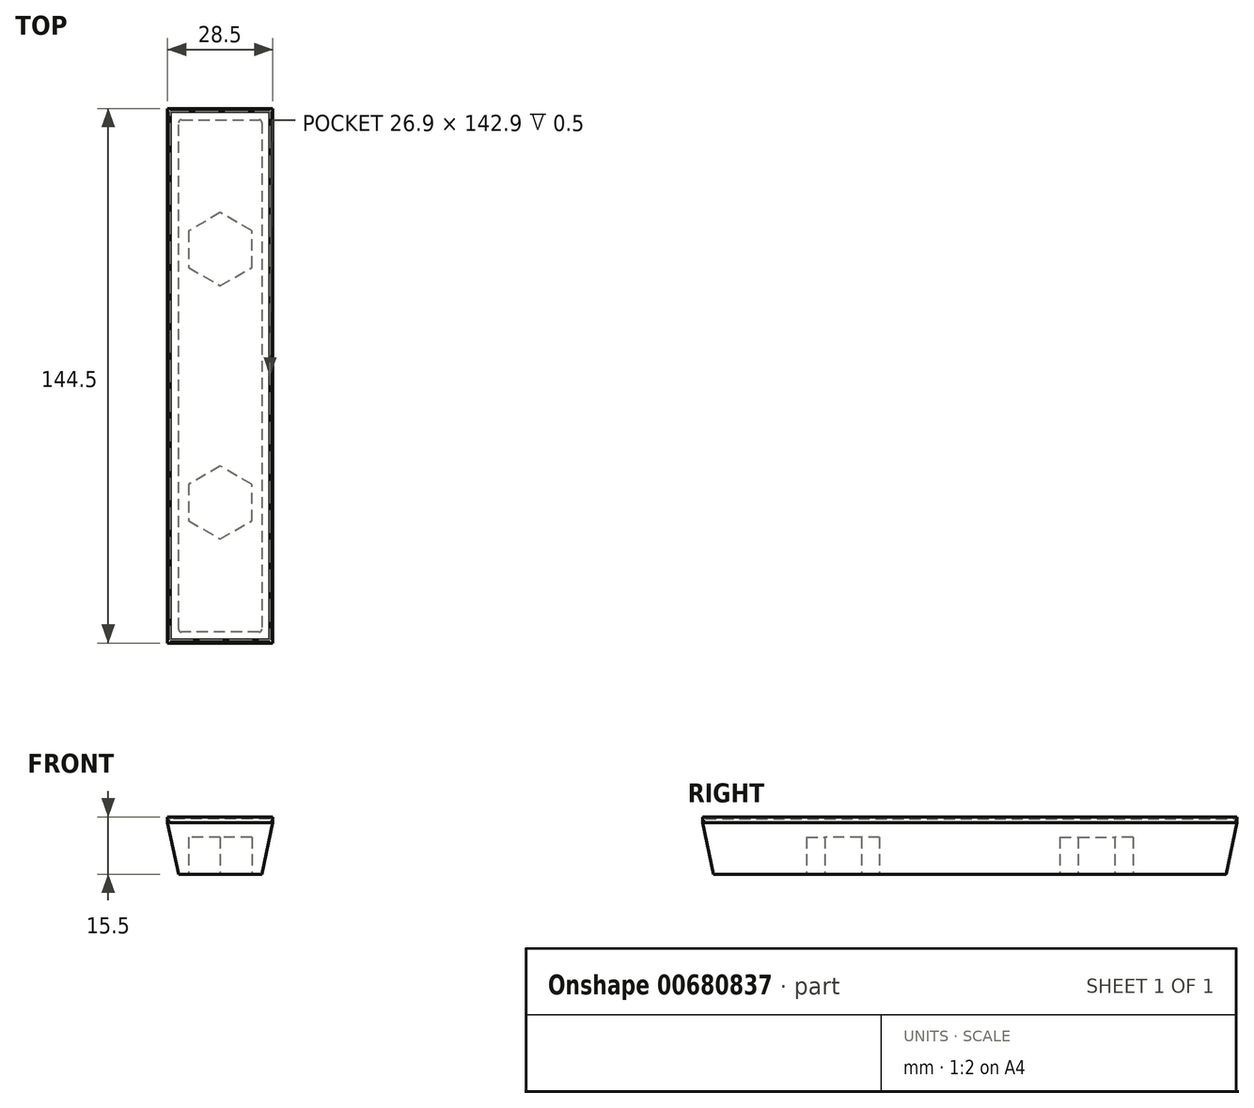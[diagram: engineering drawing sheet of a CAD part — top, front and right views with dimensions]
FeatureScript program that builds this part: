
annotation { "Feature Type Name" : "Feature", "Feature Type Description" : "" }
export const myFeature = defineFeature(function(context is Context, id is Id, definition is map)
    precondition{}
    {
        {
            assignVariable(context, id + "F0", {"name" : "h", "anyValue" : 15});
        }
        {
            var Q0;
            Q0=qCreatedBy(makeId("Top.planeOp"),FACE);
            var sketch = newSketch(context, id + "F1", { "sketchPlane" : qUnion([Q0])});
            skLineSegment(sketch, "E0.bottom", {"start": v(-14.25, -72.25) * mm, "end": v(14.25, -72.25) * mm});
            skLineSegment(sketch, "E0.top", {"start": v(-14.25, 72.25) * mm, "end": v(14.25, 72.25) * mm});
            skLineSegment(sketch, "E0.left", {"start": v(-14.25, -72.25) * mm, "end": v(-14.25, 72.25) * mm});
            skLineSegment(sketch, "E0.right", {"start": v(14.25, -72.25) * mm, "end": v(14.25, 72.25) * mm});
            skPoint(sketch, "E0.middle", {"position": v(0, 0) * mm});
            skLineSegment(sketch, "E1.bottom", {"start": v(13.45, -71.45) * mm, "end": v(-13.45, -71.45) * mm});
            skLineSegment(sketch, "E1.top", {"start": v(13.45, 71.45) * mm, "end": v(-13.45, 71.45) * mm});
            skLineSegment(sketch, "E1.left", {"start": v(13.45, -71.45) * mm, "end": v(13.45, 71.45) * mm});
            skLineSegment(sketch, "E1.right", {"start": v(-13.45, -71.45) * mm, "end": v(-13.45, 71.45) * mm});
            skSolve(sketch);
        }
        {
            var Q0;
            Q0=qSketchRegion(id+"F1",true);
            extrude(context, id + "F2", {"entities" : qUnion([Q0]), "depth" : 0.5 * mm, "offsetDistance" : 25 * mm});
        }
        {
            var Q0;
            Q0=qSketchRegion(id+"F1",true);
            var Q1;
            Q1=makeQuery(id+"F1.imprint","IMPRINT",FACE,{"disambiguationData":[TD([[makeQuery(id+"F1.imprint","IMPRINT",EDGE,{"derivedFrom":sQuery(id+"F1.wireOp",EDGE,"E1.bottom")}),-1.0]])]});
            extrude(context, id + "F3", {"entities" : qUnion([Q0, Q1]), "operationType" : NewBodyOperationType.ADD, "depth" : (-getVariable(context, 'h')) * mm, "offsetDistance" : 25 * mm});
        }
        {
            var Q0;
            Q0=makeQuery(id+"F3.opExtrude","CAP_EDGE",EDGE,{"disambiguationData":[OSD([sQuery(id+"F1.wireOp",EDGE,"E0.bottom")])],"isStart":false});
            var Q1;
            Q1=makeQuery(id+"F3.opExtrude","CAP_EDGE",EDGE,{"disambiguationData":[OSD([sQuery(id+"F1.wireOp",EDGE,"E0.right")])],"isStart":false});
            var Q2;
            Q2=makeQuery(id+"F3.opExtrude","CAP_EDGE",EDGE,{"disambiguationData":[OSD([sQuery(id+"F1.wireOp",EDGE,"E0.top")])],"isStart":false});
            var Q3;
            Q3=makeQuery(id+"F3.opExtrude","CAP_EDGE",EDGE,{"disambiguationData":[OSD([sQuery(id+"F1.wireOp",EDGE,"E0.left")])],"isStart":false});
            chamfer(context, id + "F4", {"entities" : qUnion([Q0, Q1, Q2, Q3]), "chamferType" : ChamferType.TWO_OFFSETS, "width1" : (getVariable(context, 'h') - 1) * mm, "oppositeDirection" : false, "width2" : 3 * mm, "tangentPropagation" : true});
        }
        {
            var Q0;
            Q0=makeQuery(id+"F4.opChamfer","BLEND_EDGE",EDGE,{"blendedFrom":[makeQuery(id+"F3.opExtrude","CAP_EDGE",EDGE,{"disambiguationData":[OSD([sQuery(id+"F1.wireOp",EDGE,"E0.top")])],"isStart":false}),makeQuery(id+"F3.opExtrude","CAP_EDGE",EDGE,{"disambiguationData":[OSD([sQuery(id+"F1.wireOp",EDGE,"E0.right")])],"isStart":false})],"blendedInto":[]});
            var Q1;
            Q1=makeQuery(id+"F4.opChamfer","BLEND_EDGE",EDGE,{"blendedFrom":[makeQuery(id+"F3.opExtrude","CAP_EDGE",EDGE,{"disambiguationData":[OSD([sQuery(id+"F1.wireOp",EDGE,"E0.top")])],"isStart":false}),makeQuery(id+"F3.opExtrude","CAP_EDGE",EDGE,{"disambiguationData":[OSD([sQuery(id+"F1.wireOp",EDGE,"E0.left")])],"isStart":false})],"blendedInto":[]});
            var Q2;
            Q2=makeQuery(id+"F4.opChamfer","BLEND_EDGE",EDGE,{"blendedFrom":[makeQuery(id+"F3.opExtrude","CAP_EDGE",EDGE,{"disambiguationData":[OSD([sQuery(id+"F1.wireOp",EDGE,"E0.bottom")])],"isStart":false}),makeQuery(id+"F3.opExtrude","CAP_EDGE",EDGE,{"disambiguationData":[OSD([sQuery(id+"F1.wireOp",EDGE,"E0.right")])],"isStart":false})],"blendedInto":[]});
            var Q3;
            Q3=makeQuery(id+"F4.opChamfer","BLEND_EDGE",EDGE,{"blendedFrom":[makeQuery(id+"F3.opExtrude","CAP_EDGE",EDGE,{"disambiguationData":[OSD([sQuery(id+"F1.wireOp",EDGE,"E0.bottom")])],"isStart":false}),makeQuery(id+"F3.opExtrude","CAP_EDGE",EDGE,{"disambiguationData":[OSD([sQuery(id+"F1.wireOp",EDGE,"E0.left")])],"isStart":false})],"blendedInto":[]});
            fillet(context, id + "F5", {"entities" : qUnion([Q0, Q1, Q2, Q3]), "radius" : 0.8 * mm, "tangentPropagation" : true, "allowEdgeOverflow" : false});
        }
        {
            var Q0;
            Q0=makeQuery(id+"F3.opExtrude","CAP_FACE",FACE,{"disambiguationData":[OSD([sQuery(id+"F1.wireOp",EDGE,"E0.bottom"),sQuery(id+"F1.wireOp",EDGE,"E0.top"),sQuery(id+"F1.wireOp",EDGE,"E0.left"),sQuery(id+"F1.wireOp",EDGE,"E0.right")])],"isStart":false});
            var sketch = newSketch(context, id + "F6", { "sketchPlane" : qUnion([Q0])});
            skLineSegment(sketch, "E2", {"start": v(0, -69.25) * mm, "end": v(0, 69.25) * mm, "construction": true});
            skCircle(sketch, "E3.cCircle", {"center": v(0, -34.25) * mm, "radius": 8.55 * mm, "construction": true});
            skLineSegment(sketch, "E3.0", {"start": v(0, -44.12) * mm, "end": v(-8.55, -39.19) * mm});
            skLineSegment(sketch, "E3.1", {"start": v(-8.55, -39.19) * mm, "end": v(-8.55, -29.31) * mm});
            skLineSegment(sketch, "E3.2", {"start": v(-8.55, -29.31) * mm, "end": v(0, -24.38) * mm});
            skLineSegment(sketch, "E3.3", {"start": v(0, -24.38) * mm, "end": v(8.55, -29.31) * mm});
            skLineSegment(sketch, "E3.4", {"start": v(8.55, -29.31) * mm, "end": v(8.55, -39.19) * mm});
            skLineSegment(sketch, "E3.5", {"start": v(8.55, -39.19) * mm, "end": v(0, -44.12) * mm});
            skPoint(sketch, "E3.0.midPoint", {"position": v(-4.28, -41.65) * mm});
            skCircle(sketch, "E4.cCircle", {"center": v(0, 34.25) * mm, "radius": 8.55 * mm, "construction": true});
            skLineSegment(sketch, "E4.0", {"start": v(-8.55, 29.31) * mm, "end": v(-8.55, 39.19) * mm});
            skLineSegment(sketch, "E4.1", {"start": v(-8.55, 39.19) * mm, "end": v(0, 44.12) * mm});
            skLineSegment(sketch, "E4.2", {"start": v(0, 44.12) * mm, "end": v(8.55, 39.19) * mm});
            skLineSegment(sketch, "E4.3", {"start": v(8.55, 39.19) * mm, "end": v(8.55, 29.31) * mm});
            skLineSegment(sketch, "E4.4", {"start": v(8.55, 29.31) * mm, "end": v(0, 24.38) * mm});
            skLineSegment(sketch, "E4.5", {"start": v(0, 24.38) * mm, "end": v(-8.55, 29.31) * mm});
            skPoint(sketch, "E4.0.midPoint", {"position": v(-8.55, 34.25) * mm});
            skSolve(sketch);
        }
        {
            var Q0;
            Q0=makeQuery(id+"F6.imprint","IMPRINT",FACE,{"disambiguationData":[TD([[makeQuery(id+"F6.imprint","IMPRINT",EDGE,{"derivedFrom":sQuery(id+"F6.wireOp",EDGE,"E4.0")}),-1.0]])]});
            var Q1;
            Q1=makeQuery(id+"F6.imprint","IMPRINT",FACE,{"disambiguationData":[TD([[makeQuery(id+"F6.imprint","IMPRINT",EDGE,{"derivedFrom":sQuery(id+"F6.wireOp",EDGE,"E3.0")}),-1.0]])]});
            extrude(context, id + "F7", {"entities" : qUnion([Q0, Q1]), "operationType" : NewBodyOperationType.REMOVE, "oppositeDirection" : true, "depth" : 10 * mm, "offsetDistance" : 25 * mm});
        }
    });
